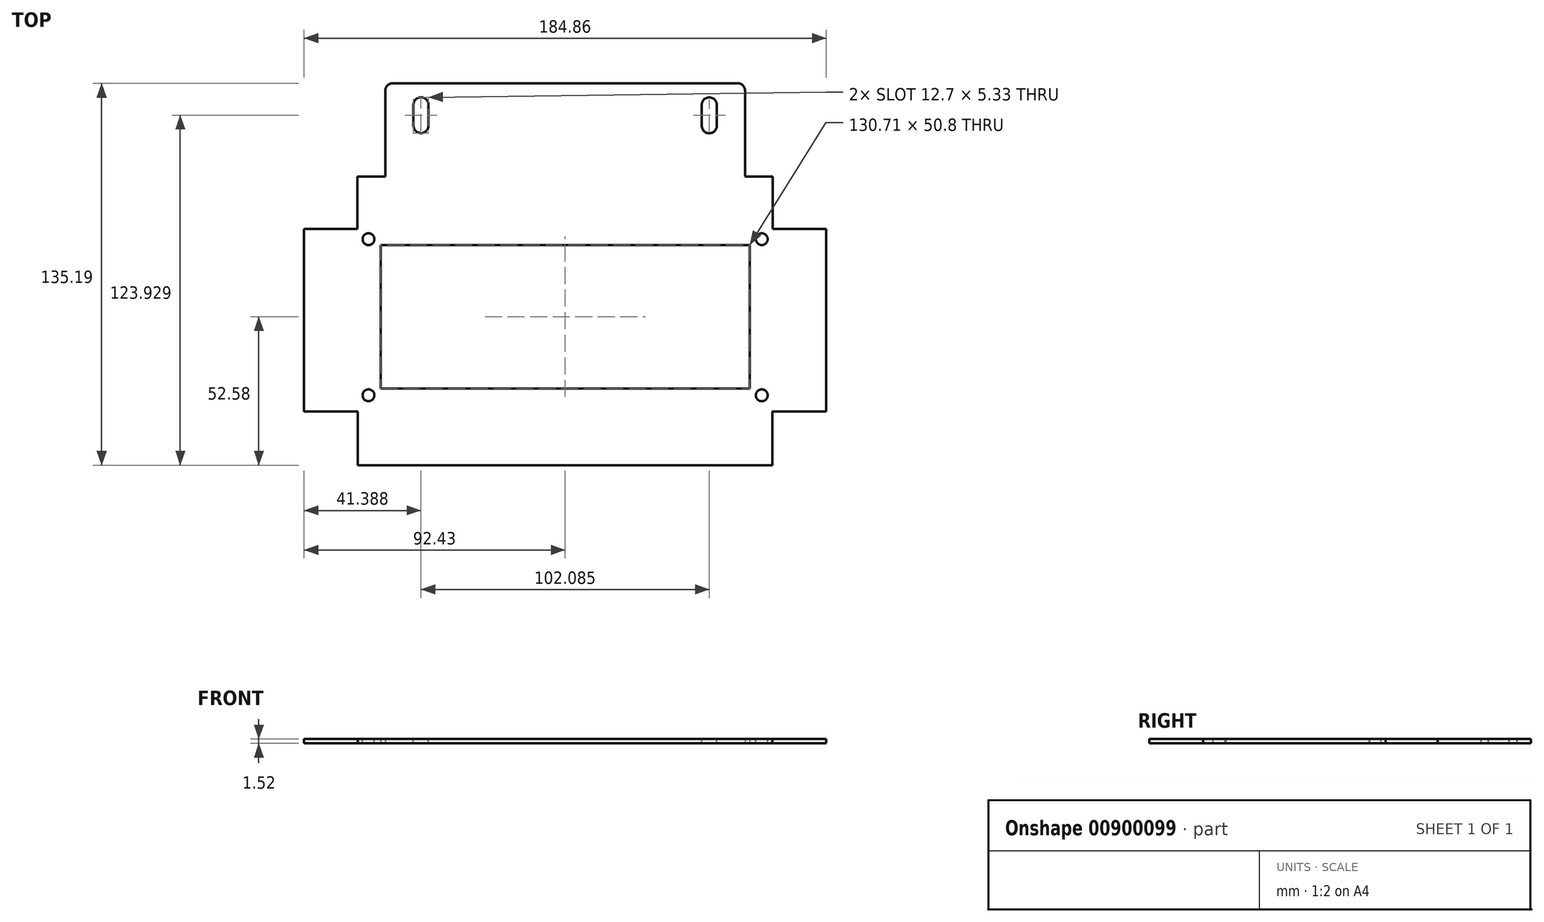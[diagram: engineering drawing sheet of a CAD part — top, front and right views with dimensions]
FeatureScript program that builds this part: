
annotation { "Feature Type Name" : "Feature", "Feature Type Description" : "" }
export const myFeature = defineFeature(function(context is Context, id is Id, definition is map)
    precondition{}
    {
        {
            var Q0;
            Q0=qCreatedBy(makeId("Top.planeOp"),FACE);
            var sketch = newSketch(context, id + "F0", { "sketchPlane" : qUnion([Q0])});
            skLineSegment(sketch, "E0.bottom", {"start": v(-65.35, -25.4) * mm, "end": v(65.35, -25.4) * mm});
            skLineSegment(sketch, "E0.top", {"start": v(-65.35, 25.4) * mm, "end": v(65.35, 25.4) * mm});
            skLineSegment(sketch, "E0.left", {"start": v(-65.35, -25.4) * mm, "end": v(-65.35, 25.4) * mm});
            skLineSegment(sketch, "E0.right", {"start": v(65.35, -25.4) * mm, "end": v(65.35, 25.4) * mm});
            skPoint(sketch, "E0.middle", {"position": v(0, 0) * mm});
            skLineSegment(sketch, "E1.bottom", {"start": v(73.38, -52.58) * mm, "end": v(-73.38, -52.58) * mm});
            skLineSegment(sketch, "E1.top", {"start": v(73.53, 49.56) * mm, "end": v(63.7, 49.56) * mm});
            skLineSegment(sketch, "E1.left", {"start": v(92.43, -33.53) * mm, "end": v(92.43, 31.11) * mm});
            skLineSegment(sketch, "E1.right", {"start": v(-92.43, -33.53) * mm, "end": v(-92.43, 31.11) * mm});
            skLineSegment(sketch, "E2.left", {"start": v(-63.7, 82.61) * mm, "end": v(-63.7, 49.56) * mm});
            skLineSegment(sketch, "E2.right", {"start": v(63.7, 82.61) * mm, "end": v(63.7, 49.56) * mm});
            skLineSegment(sketch, "E3", {"start": v(73.53, 49.56) * mm, "end": v(73.53, 31.11) * mm});
            skLineSegment(sketch, "E4", {"start": v(73.53, 31.12) * mm, "end": v(92.43, 31.12) * mm});
            skLineSegment(sketch, "E5.MirrorCS", {"start": v(-73.53, 31.11) * mm, "end": v(-92.43, 31.11) * mm});
            skLineSegment(sketch, "E6.MirrorCS", {"start": v(-73.53, 49.56) * mm, "end": v(-73.53, 31.11) * mm});
            skLineSegment(sketch, "E7", {"start": v(-63.7, 49.56) * mm, "end": v(-73.53, 49.56) * mm});
            skLineSegment(sketch, "E8", {"start": v(63.7, 82.61) * mm, "end": v(-63.7, 82.61) * mm});
            skLineSegment(sketch, "E9", {"start": v(73.38, -52.58) * mm, "end": v(73.38, -33.53) * mm});
            skLineSegment(sketch, "E10", {"start": v(73.38, -33.53) * mm, "end": v(92.43, -33.53) * mm});
            skLineSegment(sketch, "E11.MirrorCS", {"start": v(-73.38, -33.53) * mm, "end": v(-92.43, -33.53) * mm});
            skLineSegment(sketch, "E12.MirrorCS", {"start": v(-73.38, -52.58) * mm, "end": v(-73.38, -33.53) * mm});
            skLineSegment(sketch, "E13", {"start": v(0, 0) * mm, "end": v(0, 117.63) * mm, "construction": true});
            skSolve(sketch);
        }
        {
            var Q0;
            Q0=makeQuery(id+"F0.imprint","IMPRINT",FACE,{"disambiguationData":[TD([[makeQuery(id+"F0.imprint","IMPRINT",EDGE,{"derivedFrom":sQuery(id+"F0.wireOp",EDGE,"E0.bottom")}),-1.0]])]});
            extrude(context, id + "F1", {"entities" : qUnion([Q0]), "depth" : 1.52 * mm, "offsetDistance" : 25.4 * mm});
        }
        {
            var Q0;
            Q0=makeQuery(id+"F1.opExtrude","CAP_FACE",FACE,{"disambiguationData":[OSD([sQuery(id+"F0.wireOp",EDGE,"E0.bottom"),sQuery(id+"F0.wireOp",EDGE,"E0.top"),sQuery(id+"F0.wireOp",EDGE,"E0.left"),sQuery(id+"F0.wireOp",EDGE,"E0.right"),sQuery(id+"F0.wireOp",EDGE,"E1.bottom"),sQuery(id+"F0.wireOp",EDGE,"E1.top"),sQuery(id+"F0.wireOp",EDGE,"E1.left"),sQuery(id+"F0.wireOp",EDGE,"E1.right"),sQuery(id+"F0.wireOp",EDGE,"E2.left"),sQuery(id+"F0.wireOp",EDGE,"E2.right"),sQuery(id+"F0.wireOp",EDGE,"E3"),sQuery(id+"F0.wireOp",EDGE,"E4"),sQuery(id+"F0.wireOp",EDGE,"E5.MirrorCS"),sQuery(id+"F0.wireOp",EDGE,"E6.MirrorCS"),sQuery(id+"F0.wireOp",EDGE,"E7"),sQuery(id+"F0.wireOp",EDGE,"E8"),sQuery(id+"F0.wireOp",EDGE,"E9"),sQuery(id+"F0.wireOp",EDGE,"E10"),sQuery(id+"F0.wireOp",EDGE,"E11.MirrorCS"),sQuery(id+"F0.wireOp",EDGE,"E12.MirrorCS")])],"isStart":false});
            var sketch = newSketch(context, id + "F2", { "sketchPlane" : qUnion([Q0])});
            skCircle(sketch, "E14", {"center": v(69.63, -27.85) * mm, "radius": 2.1 * mm});
            skCircle(sketch, "E15", {"center": v(69.63, 27.44) * mm, "radius": 2.1 * mm});
            skLineSegment(sketch, "E16", {"start": v(0, 0) * mm, "end": v(0, 10.62) * mm});
            skCircle(sketch, "E17.MirrorC", {"center": v(-69.63, 27.44) * mm, "radius": 2.1 * mm});
            skCircle(sketch, "E18.MirrorC", {"center": v(-69.63, -27.85) * mm, "radius": 2.1 * mm});
            skSolve(sketch);
        }
        {
            var Q0;
            Q0 = qSketchRegion(id + "F2", true);
            extrude(context, id + "F3", {"entities" : qUnion([Q0]), "operationType" : NewBodyOperationType.REMOVE, "oppositeDirection" : true, "depth" : 25.4 * mm, "offsetDistance" : 25.4 * mm});
        }
        {
            var Q0;
            Q0=makeQuery(id+"F1.opExtrude","SWEPT_EDGE",EDGE,{"disambiguationData":[OSD([sQuery(id+"F0.wireOp",EDGE,"E2.right"),sQuery(id+"F0.wireOp",EDGE,"E8")])]});
            var Q1;
            Q1=makeQuery(id+"F1.opExtrude","SWEPT_EDGE",EDGE,{"disambiguationData":[OSD([sQuery(id+"F0.wireOp",EDGE,"E2.left"),sQuery(id+"F0.wireOp",EDGE,"E8")])]});
            fillet(context, id + "F4", {"entities" : qUnion([Q0, Q1]), "radius" : 2.54 * mm, "tangentPropagation" : true, "allowEdgeOverflow" : false});
        }
        {
            var Q0;
            Q0=makeQuery(id+"F1.opExtrude","CAP_FACE",FACE,{"disambiguationData":[OSD([sQuery(id+"F0.wireOp",EDGE,"E0.bottom"),sQuery(id+"F0.wireOp",EDGE,"E0.top"),sQuery(id+"F0.wireOp",EDGE,"E0.left"),sQuery(id+"F0.wireOp",EDGE,"E0.right"),sQuery(id+"F0.wireOp",EDGE,"E1.bottom"),sQuery(id+"F0.wireOp",EDGE,"E1.top"),sQuery(id+"F0.wireOp",EDGE,"E1.left"),sQuery(id+"F0.wireOp",EDGE,"E1.right"),sQuery(id+"F0.wireOp",EDGE,"E2.left"),sQuery(id+"F0.wireOp",EDGE,"E2.right"),sQuery(id+"F0.wireOp",EDGE,"E3"),sQuery(id+"F0.wireOp",EDGE,"E4"),sQuery(id+"F0.wireOp",EDGE,"E5.MirrorCS"),sQuery(id+"F0.wireOp",EDGE,"E6.MirrorCS"),sQuery(id+"F0.wireOp",EDGE,"E7"),sQuery(id+"F0.wireOp",EDGE,"E8"),sQuery(id+"F0.wireOp",EDGE,"E9"),sQuery(id+"F0.wireOp",EDGE,"E10"),sQuery(id+"F0.wireOp",EDGE,"E11.MirrorCS"),sQuery(id+"F0.wireOp",EDGE,"E12.MirrorCS")])],"isStart":false});
            var sketch = newSketch(context, id + "F5", { "sketchPlane" : qUnion([Q0])});
            skArc(sketch, "E19", {"start": v(53.7, 74.85) * mm, "mid": v(51.1, 77.63) * mm, "end": v(48.38, 74.97) * mm});
            skArc(sketch, "E20", {"start": v(48.38, 67.6) * mm, "mid": v(50.99, 64.94) * mm, "end": v(53.7, 67.49) * mm});
            skLineSegment(sketch, "E21", {"start": v(53.7, 67.49) * mm, "end": v(53.7, 74.85) * mm});
            skLineSegment(sketch, "E22", {"start": v(48.38, 67.6) * mm, "end": v(48.38, 74.97) * mm});
            skLineSegment(sketch, "E23.MirrorCS", {"start": v(-48.38, 67.67) * mm, "end": v(-48.38, 75.03) * mm});
            skArc(sketch, "E24.MirrorCS", {"start": v(-53.7, 74.92) * mm, "mid": v(-51.1, 77.7) * mm, "end": v(-48.38, 75.03) * mm});
            skArc(sketch, "E25.MirrorCS", {"start": v(-48.38, 67.67) * mm, "mid": v(-50.99, 65) * mm, "end": v(-53.7, 67.55) * mm});
            skLineSegment(sketch, "E26.MirrorCS", {"start": v(-53.7, 67.55) * mm, "end": v(-53.7, 74.92) * mm});
            skLineSegment(sketch, "E27", {"start": v(-51.04, 75.03) * mm, "end": v(-51.04, 67.67) * mm});
            skSolve(sketch);
        }
        {
            var Q0;
            Q0 = qSketchRegion(id + "F5", true);
            extrude(context, id + "F6", {"entities" : qUnion([Q0]), "operationType" : NewBodyOperationType.REMOVE, "oppositeDirection" : true, "depth" : 25.4 * mm, "offsetDistance" : 25.4 * mm});
        }
    });
